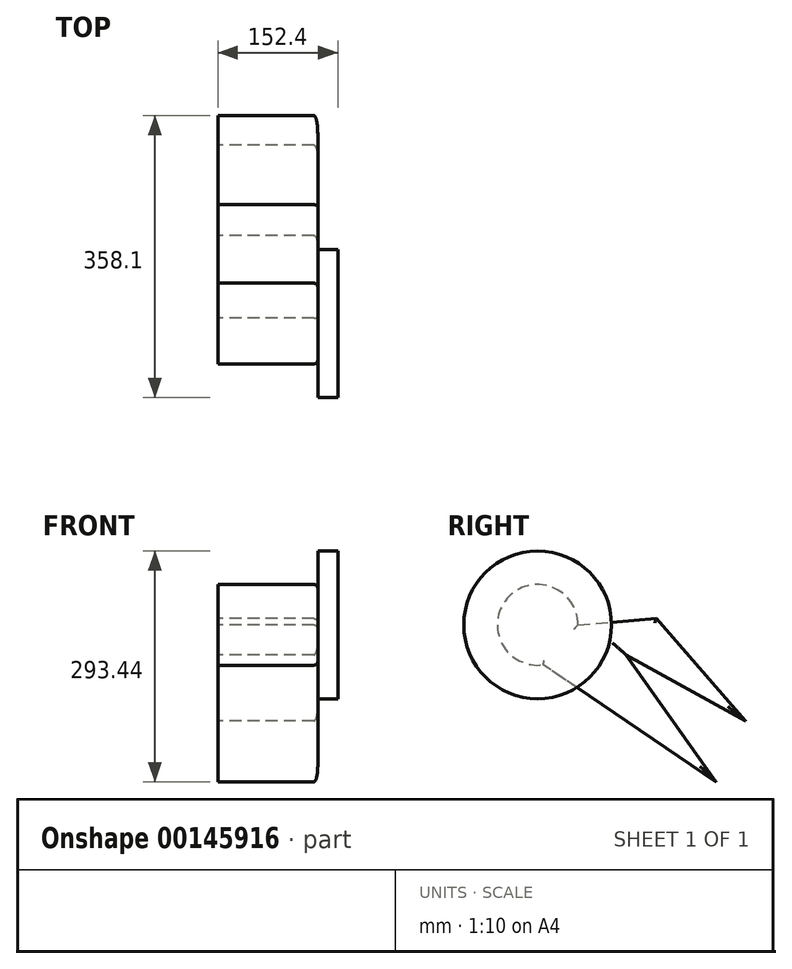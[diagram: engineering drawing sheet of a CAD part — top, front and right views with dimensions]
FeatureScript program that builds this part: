
annotation { "Feature Type Name" : "Feature", "Feature Type Description" : "" }
export const myFeature = defineFeature(function(context is Context, id is Id, definition is map)
    precondition{}
    {
        {
            var Q0;
            Q0=qCreatedBy(makeId("Right.planeOp"),FACE);
            var sketch = newSketch(context, id + "F0", { "sketchPlane" : qUnion([Q0])});
            skArc(sketch, "E0", {"start": v(51.24, 0) * mm, "mid": v(-38.67, 33.62) * mm, "end": v(7.13, -50.74) * mm});
            skLineSegment(sketch, "E1", {"start": v(51.24, 0) * mm, "end": v(150.88, 7.94) * mm});
            skLineSegment(sketch, "E2", {"start": v(150.88, 7.94) * mm, "end": v(264.2, -121.97) * mm});
            skLineSegment(sketch, "E3", {"start": v(264.2, -121.97) * mm, "end": v(112.08, -38.09) * mm});
            skLineSegment(sketch, "E4", {"start": v(112.08, -38.09) * mm, "end": v(226.63, -199.54) * mm});
            skLineSegment(sketch, "E5", {"start": v(226.63, -199.54) * mm, "end": v(6.77, -50.5) * mm});
            skSolve(sketch);
        }
        {
            var Q0;
            Q0 = qSketchRegion(id + "F0", true);
            extrude(context, id + "F1", {"entities" : qUnion([Q0]), "depth" : 127 * mm});
        }
        {
            var Q0;
            Q0=makeQuery(id+"F1.opExtrude","CAP_EDGE",EDGE,{"disambiguationData":[OSD([sQuery(id+"F0.wireOp",EDGE,"E1")])],"isStart":false});
            var Q1;
            Q1=makeQuery(id+"F1.opExtrude","CAP_FACE",FACE,{"disambiguationData":[OSD([sQuery(id+"F0.wireOp",EDGE,"E0"),sQuery(id+"F0.wireOp",EDGE,"E1"),sQuery(id+"F0.wireOp",EDGE,"E2"),sQuery(id+"F0.wireOp",EDGE,"E3"),sQuery(id+"F0.wireOp",EDGE,"E4"),sQuery(id+"F0.wireOp",EDGE,"E5")])],"isStart":false});
            var Q2;
            Q2=makeQuery(id+"F1.opExtrude","CAP_FACE",FACE,{"disambiguationData":[OSD([sQuery(id+"F0.wireOp",EDGE,"E0"),sQuery(id+"F0.wireOp",EDGE,"E1"),sQuery(id+"F0.wireOp",EDGE,"E2"),sQuery(id+"F0.wireOp",EDGE,"E3"),sQuery(id+"F0.wireOp",EDGE,"E4"),sQuery(id+"F0.wireOp",EDGE,"E5")])],"isStart":false});
            fillet(context, id + "F2", {"entities" : qUnion([Q0, Q1, Q2]), "radius" : 5.08 * mm, "tangentPropagation" : true, "allowEdgeOverflow" : false});
        }
        {
            var Q0;
            Q0=makeQuery(id+"F1.opExtrude","CAP_FACE",FACE,{"disambiguationData":[OSD([sQuery(id+"F0.wireOp",EDGE,"E0"),sQuery(id+"F0.wireOp",EDGE,"E1"),sQuery(id+"F0.wireOp",EDGE,"E2"),sQuery(id+"F0.wireOp",EDGE,"E3"),sQuery(id+"F0.wireOp",EDGE,"E4"),sQuery(id+"F0.wireOp",EDGE,"E5")])],"isStart":false});
            var sketch = newSketch(context, id + "F3", { "sketchPlane" : qUnion([Q0])});
            skCircle(sketch, "E6", {"center": v(0, 0) * mm, "radius": 93.9 * mm});
            skSolve(sketch);
        }
        {
            var Q0;
            Q0 = qSketchRegion(id + "F3", true);
            extrude(context, id + "F4", {"entities" : qUnion([Q0]), "depth" : 25.4 * mm});
        }
    });
